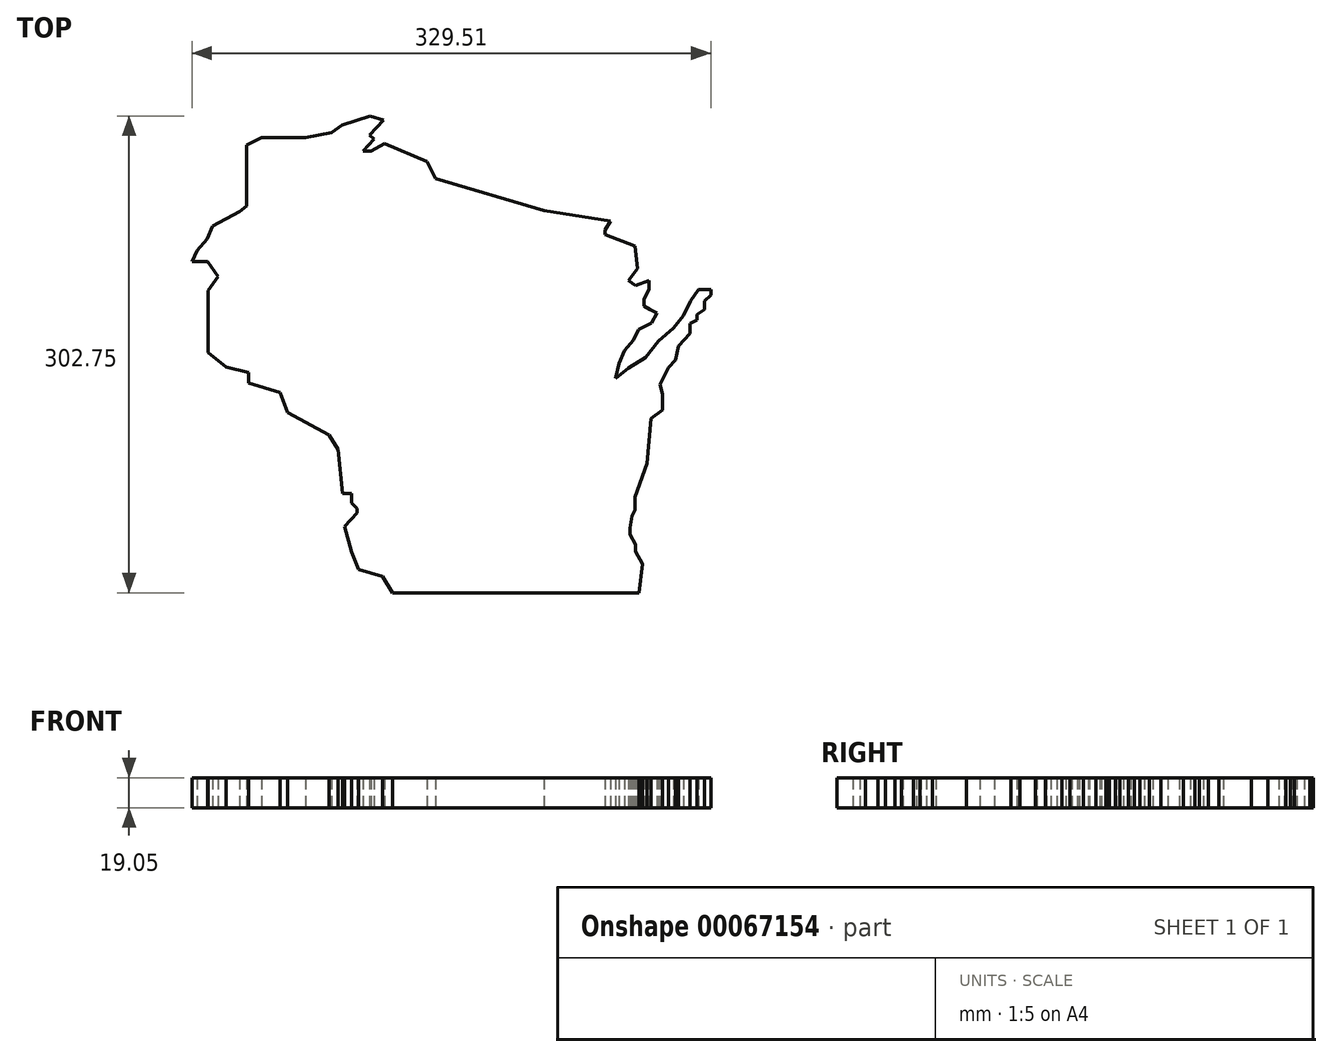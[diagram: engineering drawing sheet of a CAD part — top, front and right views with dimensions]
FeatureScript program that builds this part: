
annotation { "Feature Type Name" : "Feature", "Feature Type Description" : "" }
export const myFeature = defineFeature(function(context is Context, id is Id, definition is map)
    precondition{}
    {
        {
            var Q0;
            Q0=qCreatedBy(makeId("Top.planeOp"),FACE);
            var sketch = newSketch(context, id + "F0", { "sketchPlane" : qUnion([Q0])});
            skLineSegment(sketch, "E0", {"start": v(130.08, 0) * mm, "end": v(283.88, 0) * mm});
            skLineSegment(sketch, "E1", {"start": v(283.88, 0) * mm, "end": v(286.13, 18.15) * mm});
            skLineSegment(sketch, "E2", {"start": v(286.13, 18.15) * mm, "end": v(281.6, 26.12) * mm});
            skLineSegment(sketch, "E3", {"start": v(281.6, 26.12) * mm, "end": v(281.6, 30.82) * mm});
            skLineSegment(sketch, "E4", {"start": v(281.6, 30.82) * mm, "end": v(278.16, 36.98) * mm});
            skLineSegment(sketch, "E5", {"start": v(278.16, 36.98) * mm, "end": v(278.16, 41.15) * mm});
            skLineSegment(sketch, "E6", {"start": v(278.16, 41.15) * mm, "end": v(279.43, 48.75) * mm});
            skLineSegment(sketch, "E7", {"start": v(279.43, 48.75) * mm, "end": v(281.24, 52.74) * mm});
            skLineSegment(sketch, "E8", {"start": v(281.24, 52.74) * mm, "end": v(281.24, 60.88) * mm});
            skLineSegment(sketch, "E9", {"start": v(281.24, 60.88) * mm, "end": v(289.03, 82.25) * mm});
            skLineSegment(sketch, "E10", {"start": v(289.03, 82.25) * mm, "end": v(291.43, 110.67) * mm});
            skLineSegment(sketch, "E11", {"start": v(291.43, 110.67) * mm, "end": v(298.73, 116.19) * mm});
            skLineSegment(sketch, "E12", {"start": v(298.73, 116.19) * mm, "end": v(298.73, 126.12) * mm});
            skLineSegment(sketch, "E13", {"start": v(298.73, 126.12) * mm, "end": v(297.1, 132.37) * mm});
            skLineSegment(sketch, "E14", {"start": v(297.1, 132.37) * mm, "end": v(302.62, 143.03) * mm});
            skLineSegment(sketch, "E15", {"start": v(302.62, 143.03) * mm, "end": v(307.22, 148) * mm});
            skLineSegment(sketch, "E16", {"start": v(307.22, 148) * mm, "end": v(309.05, 156.63) * mm});
            skLineSegment(sketch, "E17", {"start": v(309.05, 156.63) * mm, "end": v(316.4, 164.72) * mm});
            skLineSegment(sketch, "E18", {"start": v(316.4, 164.72) * mm, "end": v(316.4, 170.97) * mm});
            skLineSegment(sketch, "E19", {"start": v(316.4, 170.97) * mm, "end": v(320.63, 173.18) * mm});
            skLineSegment(sketch, "E20", {"start": v(320.63, 173.18) * mm, "end": v(320.63, 176.85) * mm});
            skLineSegment(sketch, "E21", {"start": v(320.63, 176.85) * mm, "end": v(325.41, 179.98) * mm});
            skLineSegment(sketch, "E22", {"start": v(325.41, 179.98) * mm, "end": v(325.41, 185.27) * mm});
            skLineSegment(sketch, "E23", {"start": v(325.41, 185.27) * mm, "end": v(329.51, 189.18) * mm});
            skLineSegment(sketch, "E24", {"start": v(329.51, 189.18) * mm, "end": v(329.51, 192.6) * mm});
            skLineSegment(sketch, "E25", {"start": v(329.51, 192.6) * mm, "end": v(321.6, 192.6) * mm});
            skLineSegment(sketch, "E26", {"start": v(321.6, 192.6) * mm, "end": v(316.71, 185.27) * mm});
            skLineSegment(sketch, "E27", {"start": v(316.71, 185.27) * mm, "end": v(312.31, 176.23) * mm});
            skLineSegment(sketch, "E28", {"start": v(312.31, 176.23) * mm, "end": v(305.96, 168.17) * mm});
            skLineSegment(sketch, "E29", {"start": v(305.96, 168.17) * mm, "end": v(296.2, 159.86) * mm});
            skLineSegment(sketch, "E30", {"start": v(296.2, 159.86) * mm, "end": v(288.13, 149.36) * mm});
            skLineSegment(sketch, "E31", {"start": v(288.13, 149.36) * mm, "end": v(277.14, 142.76) * mm});
            skLineSegment(sketch, "E32", {"start": v(277.14, 142.76) * mm, "end": v(269.08, 136.17) * mm});
            skLineSegment(sketch, "E33", {"start": v(269.08, 136.17) * mm, "end": v(271.27, 145.7) * mm});
            skLineSegment(sketch, "E34", {"start": v(271.27, 145.7) * mm, "end": v(274.7, 154) * mm});
            skLineSegment(sketch, "E35", {"start": v(274.7, 154) * mm, "end": v(280.31, 160.6) * mm});
            skLineSegment(sketch, "E36", {"start": v(280.31, 160.6) * mm, "end": v(283.73, 167.19) * mm});
            skLineSegment(sketch, "E37", {"start": v(283.73, 167.19) * mm, "end": v(291.8, 171.34) * mm});
            skLineSegment(sketch, "E38", {"start": v(291.8, 171.34) * mm, "end": v(295.21, 177.7) * mm});
            skLineSegment(sketch, "E39", {"start": v(295.21, 177.7) * mm, "end": v(290.9, 180.02) * mm});
            skLineSegment(sketch, "E40", {"start": v(290.9, 180.02) * mm, "end": v(287.15, 182.1) * mm});
            skLineSegment(sketch, "E41", {"start": v(287.15, 182.1) * mm, "end": v(287.15, 186.73) * mm});
            skLineSegment(sketch, "E42", {"start": v(287.15, 186.73) * mm, "end": v(290.33, 192.6) * mm});
            skLineSegment(sketch, "E43", {"start": v(290.33, 192.6) * mm, "end": v(290.33, 198.46) * mm});
            skLineSegment(sketch, "E44", {"start": v(290.33, 198.46) * mm, "end": v(281.53, 195.28) * mm});
            skLineSegment(sketch, "E45", {"start": v(281.53, 195.28) * mm, "end": v(277.38, 198.21) * mm});
            skLineSegment(sketch, "E46", {"start": v(277.38, 198.21) * mm, "end": v(282.84, 205.94) * mm});
            skLineSegment(sketch, "E47", {"start": v(282.84, 205.94) * mm, "end": v(281.4, 220.3) * mm});
            skLineSegment(sketch, "E48", {"start": v(281.4, 220.3) * mm, "end": v(262.46, 227.5) * mm});
            skLineSegment(sketch, "E49", {"start": v(262.46, 227.5) * mm, "end": v(262.46, 230.3) * mm});
            skLineSegment(sketch, "E50", {"start": v(262.46, 230.3) * mm, "end": v(265.8, 236.1) * mm});
            skLineSegment(sketch, "E51", {"start": v(265.8, 236.1) * mm, "end": v(223.52, 242.76) * mm});
            skLineSegment(sketch, "E52", {"start": v(223.52, 242.76) * mm, "end": v(154.82, 263.22) * mm});
            skLineSegment(sketch, "E53", {"start": v(154.82, 263.22) * mm, "end": v(149.38, 273.82) * mm});
            skLineSegment(sketch, "E54", {"start": v(149.38, 273.82) * mm, "end": v(122.45, 285.28) * mm});
            skLineSegment(sketch, "E55", {"start": v(122.45, 285.28) * mm, "end": v(113.85, 280.7) * mm});
            skLineSegment(sketch, "E56", {"start": v(113.85, 280.7) * mm, "end": v(108.7, 280.7) * mm});
            skLineSegment(sketch, "E57", {"start": v(108.7, 280.7) * mm, "end": v(115.57, 288.14) * mm});
            skLineSegment(sketch, "E58", {"start": v(115.57, 288.14) * mm, "end": v(112.79, 290.71) * mm});
            skLineSegment(sketch, "E59", {"start": v(112.79, 290.71) * mm, "end": v(121.7, 300.37) * mm});
            skLineSegment(sketch, "E60", {"start": v(121.7, 300.37) * mm, "end": v(113, 302.75) * mm});
            skLineSegment(sketch, "E61", {"start": v(113, 302.75) * mm, "end": v(95.23, 297.02) * mm});
            skLineSegment(sketch, "E62", {"start": v(95.23, 297.02) * mm, "end": v(88.64, 292.15) * mm});
            skLineSegment(sketch, "E63", {"start": v(88.64, 292.15) * mm, "end": v(72.03, 289) * mm});
            skLineSegment(sketch, "E64", {"start": v(72.03, 289) * mm, "end": v(44.24, 289) * mm});
            skLineSegment(sketch, "E65", {"start": v(44.24, 289) * mm, "end": v(34.8, 284.44) * mm});
            skLineSegment(sketch, "E66", {"start": v(34.8, 284.44) * mm, "end": v(34.8, 245.54) * mm});
            skLineSegment(sketch, "E67", {"start": v(34.8, 245.54) * mm, "end": v(30.28, 242) * mm});
            skLineSegment(sketch, "E68", {"start": v(30.28, 242) * mm, "end": v(13.2, 232.97) * mm});
            skLineSegment(sketch, "E69", {"start": v(13.2, 232.97) * mm, "end": v(9.45, 224.56) * mm});
            skLineSegment(sketch, "E70", {"start": v(9.45, 224.56) * mm, "end": v(3.28, 217.5) * mm});
            skLineSegment(sketch, "E71", {"start": v(3.28, 217.5) * mm, "end": v(0, 210.46) * mm});
            skLineSegment(sketch, "E72", {"start": v(0, 210.46) * mm, "end": v(9.89, 210.46) * mm});
            skLineSegment(sketch, "E73", {"start": v(9.89, 210.46) * mm, "end": v(16.5, 200.76) * mm});
            skLineSegment(sketch, "E74", {"start": v(16.5, 200.76) * mm, "end": v(10.1, 191.95) * mm});
            skLineSegment(sketch, "E75", {"start": v(10.1, 191.95) * mm, "end": v(10.1, 152.72) * mm});
            skLineSegment(sketch, "E76", {"start": v(10.1, 152.72) * mm, "end": v(21.74, 143.3) * mm});
            skPoint(sketch, "E76.endSnap0", {"position": v(21.74, 237.5) * mm});
            skLineSegment(sketch, "E77", {"start": v(21.74, 143.3) * mm, "end": v(35.96, 139.82) * mm});
            skLineSegment(sketch, "E78", {"start": v(35.96, 139.82) * mm, "end": v(35.96, 133.2) * mm});
            skLineSegment(sketch, "E79", {"start": v(35.96, 133.2) * mm, "end": v(55.8, 127.3) * mm});
            skLineSegment(sketch, "E80", {"start": v(55.8, 127.3) * mm, "end": v(60.66, 114.42) * mm});
            skLineSegment(sketch, "E81", {"start": v(60.66, 114.42) * mm, "end": v(87.1, 100.15) * mm});
            skLineSegment(sketch, "E82", {"start": v(87.1, 100.15) * mm, "end": v(92.64, 91.07) * mm});
            skLineSegment(sketch, "E83", {"start": v(92.64, 91.07) * mm, "end": v(95.66, 62.98) * mm});
            skLineSegment(sketch, "E84", {"start": v(95.66, 62.98) * mm, "end": v(101.23, 62.98) * mm});
            skLineSegment(sketch, "E85", {"start": v(101.23, 62.98) * mm, "end": v(101.23, 56.95) * mm});
            skLineSegment(sketch, "E86", {"start": v(101.23, 56.95) * mm, "end": v(104.94, 53.46) * mm});
            skLineSegment(sketch, "E87", {"start": v(104.94, 53.46) * mm, "end": v(104.94, 50.68) * mm});
            skLineSegment(sketch, "E88", {"start": v(104.94, 50.68) * mm, "end": v(97.05, 42.09) * mm});
            skLineSegment(sketch, "E89", {"start": v(97.05, 42.09) * mm, "end": v(101.23, 26.07) * mm});
            skLineSegment(sketch, "E90", {"start": v(101.23, 26.07) * mm, "end": v(105.64, 14.7) * mm});
            skLineSegment(sketch, "E91", {"start": v(105.64, 14.7) * mm, "end": v(121.17, 10.37) * mm});
            skLineSegment(sketch, "E92", {"start": v(121.17, 10.37) * mm, "end": v(127.37, 0) * mm});
            skLineSegment(sketch, "E93", {"start": v(127.37, 0) * mm, "end": v(130.08, 0) * mm});
            skSolve(sketch);
        }
        {
            var Q0;
            Q0=makeQuery(id+"F0.imprint","IMPRINT",FACE,{"disambiguationData":[TD([[makeQuery(id+"F0.imprint","IMPRINT",EDGE,{"derivedFrom":sQuery(id+"F0.wireOp",EDGE,"E0")}),1.0]])]});
            extrude(context, id + "F1", {"entities" : qUnion([Q0]), "depth" : 19.05 * mm});
        }
    });
